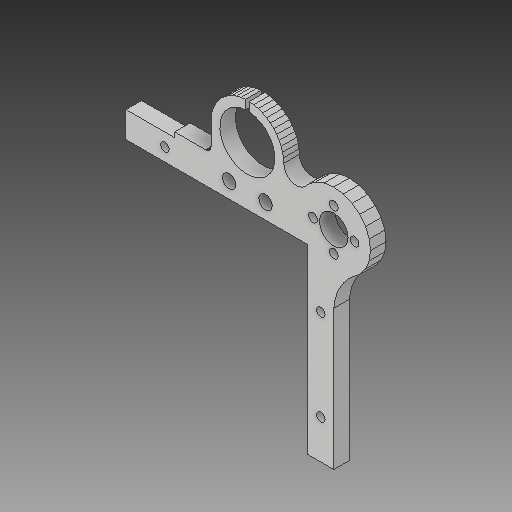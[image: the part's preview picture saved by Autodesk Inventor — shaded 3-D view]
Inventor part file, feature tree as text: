
AUTODESK INVENTOR PART (.ipt)
format: ipt  version: 2017 (Build 210142000, 142)  size: 450,048 bytes
history: native  units: mm
features: sketch x4, hole x3, extrude x1
ambient origin geometry x8: Origin, YZ Plane, XZ Plane, XY Plane, X Axis, Y Axis, Z Axis, Center Point
bodies: Solid1 (feature_tree)
feature tree (8):
  extrude  "Extrusion1"  [1 undecoded]
  hole  "Hole1"  [1 undecoded]
  hole  "Hole2"  [1 undecoded]
  hole  "Hole3"  [1 undecoded]
  sketch  "Sketch1"  dims[d0=6.0mm d1=0.0mm]
  sketch  "Sketch2"  dims[d2=3.3mm d3=6.0mm d4=4.0mm d5=2.0mm d6=90.0deg d7=8.0mm d8=20.594885mm]
  sketch  "Sketch3"  dims[d9=3.4mm d10=6.0mm d11=4.0mm d12=2.0mm d13=90.0deg d14=8.0mm d15=20.594885mm]
  sketch  "Sketch4"  dims[d16=21.2mm d17=6.0mm d18=4.0mm d19=2.0mm d20=90.0deg d21=8.0mm d22=20.594885mm]
note: 4 required parameter values undecoded (feature->parameter linkage not recoverable at this tier; creation-order binding heuristic only, values carry confidence <= 0.55)
